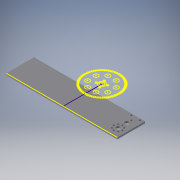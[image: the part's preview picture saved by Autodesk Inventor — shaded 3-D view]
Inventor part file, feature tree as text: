
AUTODESK INVENTOR PART (.ipt)
format: ipt  version: 2016 (Build 200138000, 138)  size: 252,416 bytes
history: native  units: in
note: dims shown in document units (in); Inventor stores cm internally (conversion verified against a paired STEP export)
features: sketch x4, reference x4, extrude x3
ambient origin geometry x8: Origin, YZ Plane, XZ Plane, XY Plane, X Axis, Y Axis, Z Axis, Center Point
bodies: Solid1 (feature_tree)
feature tree (11):
  extrude  "Extrusion1"  Depth=8.0in
  extrude  "Extrusion2"  Depth=0.13in TaperAngle=0.0deg
  sketch  "Sketch3"  dims[d6=0.5625in d7=0.0in]
  extrude  "Extrusion3"  [1 undecoded]
  sketch  "Sketch1"  dims[d0=2.0in d1=8.0in]
  sketch  "Sketch2"  dims[d2=0.13in d3=0.0in d4=0.8075in d5=0.0in]
  reference  "Reference1"
  reference  "Reference2"
  reference  "Reference3"
  sketch  "Sketch4"
  reference  "Reference4"
note: 1 required parameter value undecoded (feature->parameter linkage not recoverable at this tier; creation-order binding heuristic only, values carry confidence <= 0.55)
